# Revit family: n56e with pipe cover(1)
name_source: partatom
category: Generic Models
units: mm (PartAtom-declared; Revit-internal decimal feet)

## family parameters
Can host rebar = No
Cut with Voids When Loaded = No
Host = Face
Part Type = Normal
Room Calculation Point = No
Round Connector Dimension = Use Diameter
Shared = No

## types (2) — shared parameters
Cold (from centreline) = 10 mm  [stored 0.0328084 ft]
Cold Inlet (from back of unit) = 76 mm
Cold Water Inlet = R¾ (20 mm)
Condensate = R¾ (15 mm)
Condensate Outlet (from centreline) = 196 mm
Conensate Outlet (from back of unit) = 120 mm  [stored 0.393701 ft]
Default Elevation = 1219 mm
Efficiency = 97%
Gas (from centreline) = 142 mm  [stored 0.465879 ft]
Gas Inlet (from back of unit) = 57 mm
Gas Supply = R¾ (20 mm)
Hot Outlet (from back of unit) = 142 mm  [stored 0.465879 ft]
Hot Outlet (from centreline) = 130 mm
Hot Water Capacity = 1.5 - 37 L/min
Hot Water Outlet = R¾ (20 mm)
Ingition System = Direct electronic ignition
Ingress Protection Rating = IPX5
Input = 16 - 209 MJ/h
Line Pressure Maximum = 3.5 kPa (maximum standing pressure under abnormal intermittent conditions is 5.0 kPa)
Minimum Operating Presure = 10 kPa
Minimum Water Flow = 1.5 L/min
NOx af = Less than 50 ppm
Noise Level = 54 dB(A)
Nominal Operating Pressure = 300 - 1000 kPa
Nominal Water Capacity = 32 L/min @ 25° rise
Ouput = 56 kW
PRV (from back of unit) = 180 mm  [stored 0.590551 ft]
PRV (from centreline) = 30 mm  [stored 0.0984252 ft]
Power Consumption (Automatic Frost Protection) = 154 W
Power Consumption (Standby) = 2.4 W
Weight = 29.00 kg

## per-type parameters (varying)
| type | Constraint | Description | Line Pressures | Manufacturer | Model | Power Consumption (Normal) | URL |
| N56eN | 1 | Condensing gas continous flow water heaters | 1.13 - 3.0 kPa | Rinnai | N-Series | 70 W | https://rinnai.co.nz |
| N56eL | 2 |  | 2.75 - 3.0 kPa |  |  | 85 W |  |

note: [stored X ft] marks values corroborated as IEEE doubles in the binary element streams (Revit-internal decimal feet)

## geometry (parser evidence)
native form markers: Sweep x9
no freeform markers — native parametric forms only
